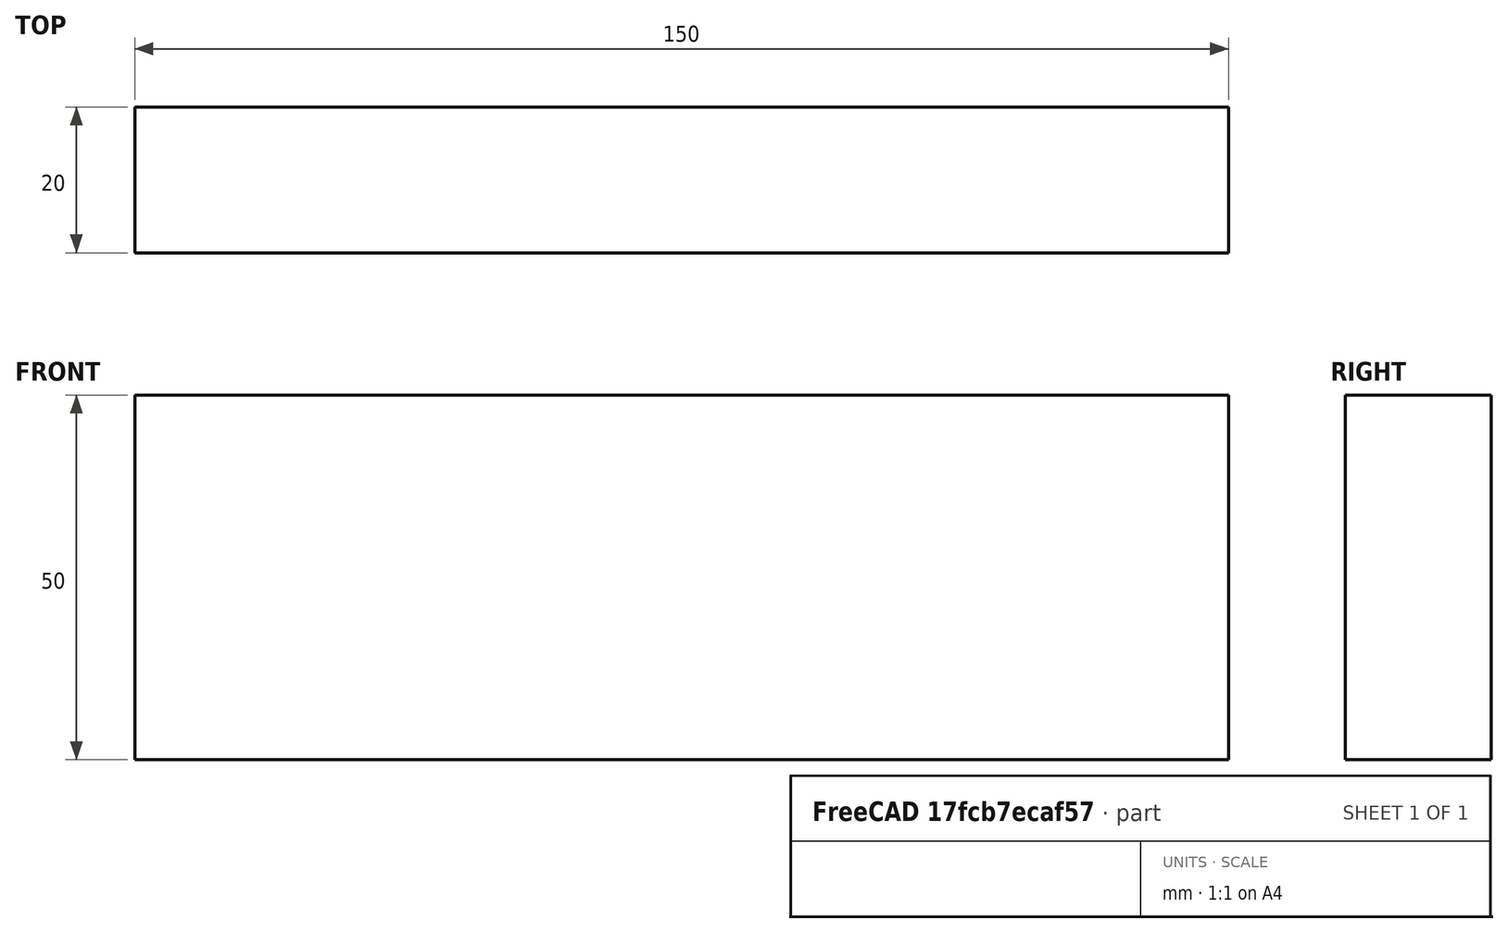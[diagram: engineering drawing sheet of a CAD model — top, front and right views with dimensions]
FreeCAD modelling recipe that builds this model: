
FCSTD DOCUMENT  (FreeCAD 0.15R4671 (Git))
Label: Flat Bar 150x20 EN10058 S235JR
License: All rights reserved
LicenseURL: http://en.wikipedia.org/wiki/All_rights_reserved
objects: Sketcher::SketchObject×1, Part::Extrusion×1
note: 2 computed .brp shape members not serialized (recipe doc carries the construction recipe); baked Part::Feature solids carry a one-line shape summary decoded from their .brp

FEATURE [Sketcher::SketchObject] Sketch
  sketch-geometry (4):
    g0: LineSegment StartX=-75 StartY=-10 StartZ=0 EndX=75 EndY=-10 EndZ=0
    g1: LineSegment StartX=75 StartY=-10 StartZ=0 EndX=75 EndY=10 EndZ=0
    g2: LineSegment StartX=75 StartY=10 StartZ=0 EndX=-75 EndY=10 EndZ=0
    g3: LineSegment StartX=-75 StartY=10 StartZ=0 EndX=-75 EndY=-10 EndZ=0
  constraints (12):
    c: Coincident(g0,g1)
    c: Coincident(g1,g2)
    c: Coincident(g2,g3)
    c: Coincident(g3,g0)
    c: Horizontal(g0)
    c: Horizontal(g2)
    c: Vertical(g1)
    c: Vertical(g3)
    c: Symmetric(g1,g2,g-2)
    c: Symmetric(g0,g1,g-1)
    c: DistanceY(g1) = 20
    c: DistanceX(g0) = 150
FEATURE [Part::Extrusion] Extrude  label="Flat Bar 150x20 EN10058 S235JR"
  Base = -> Sketch
  Dir = (0,0,50)
  Solid = true
